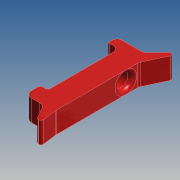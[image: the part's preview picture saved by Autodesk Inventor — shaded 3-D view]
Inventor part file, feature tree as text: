
AUTODESK INVENTOR PART (.ipt)
format: ipt  version: 2015 SP1 (Build 190203100, 203)  size: 306,688 bytes
history: native  units: mm
features: fillet x10, extrude x1, hole x1, sketch x1
ambient origin geometry x8: Origin, YZ Plane, XZ Plane, XY Plane, X Axis, Y Axis, Z Axis, Center Point
bodies: Solid1 (feature_tree)
feature tree (13):
  extrude  "Extrusion1"  Depth=2.0mm
  fillet  "Fillet1"  Radius=20.0mm
  fillet  "Fillet2"  Radius=22.0mm
  fillet  "Fillet3"  Radius=30.0mm
  fillet  "Fillet4"  Radius=4.1mm
  fillet  "Fillet5"  Radius=3.0mm
  hole  "Hole1"  [1 undecoded]
  fillet  "Fillet6"  Radius=6.0mm
  fillet  "Fillet8"  Radius=9.0mm
  fillet  "Fillet9"  [1 undecoded]
  fillet  "Fillet10"  Radius=16.0mm
  fillet  "Fillet11"  Radius=7.0mm
  sketch  "Sketch2"  dims[d1=3.0mm d2=5.0mm d3=14.0mm d4=20.0mm d5=22.0mm d6=30.0mm d7=4.1mm d8=3.0mm d9=25.0mm d10=6.0mm d11=9.0mm d12=0.0mm d13=16.0mm d14=7.0mm d15=3.5mm d16=120.0deg d17=1.308997mm d19=5.0mm d20=5.0mm d21=1.0mm d22=1.0mm d23=1.0mm d24=9.8mm d25=0.0mm d26=0.5mm d27=1.0mm d28=3.0mm d29=2.0mm d30=1.0mm d32=6.0mm d33=6.0mm d34=4.0mm d35=2.0mm d36=90.0deg d37=8.0mm d38=20.594885mm d39=2.0mm d40=45.0deg d41=3.0mm d42=10.0mm d43=5.0mm d44=12.0mm d46=1.5mm d47=1.0mm d48=2.0mm d49=1.0mm d50=2.0mm]
note: 2 required parameter values undecoded (feature->parameter linkage not recoverable at this tier; creation-order binding heuristic only, values carry confidence <= 0.55)
